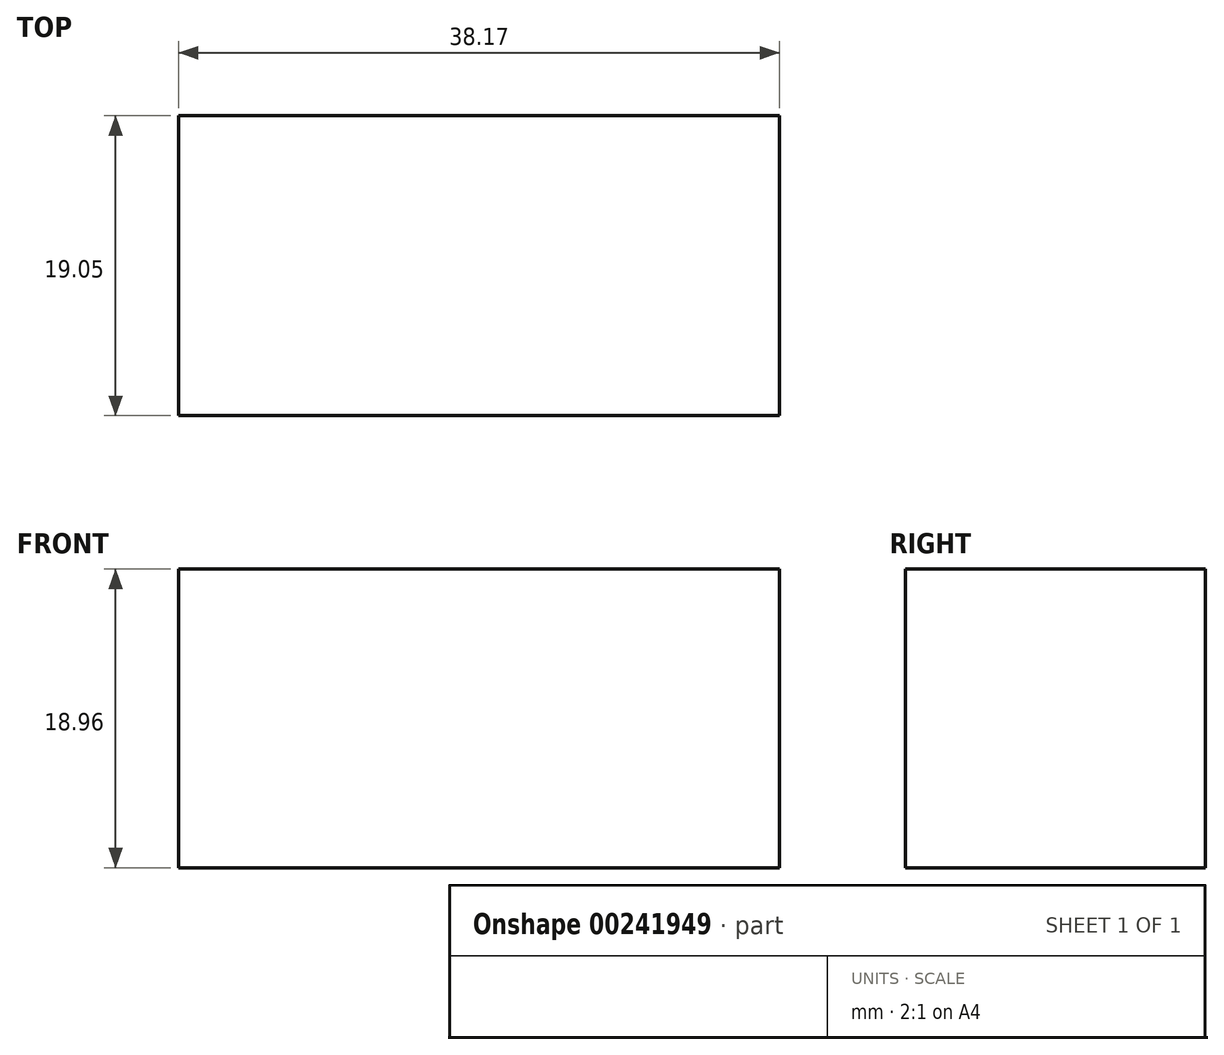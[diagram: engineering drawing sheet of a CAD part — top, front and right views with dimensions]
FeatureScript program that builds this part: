
annotation { "Feature Type Name" : "Feature", "Feature Type Description" : "" }
export const myFeature = defineFeature(function(context is Context, id is Id, definition is map)
    precondition{}
    {
        {
            var Q0;
            Q0=qCreatedBy(makeId("Front.planeOp"),FACE);
            var sketch = newSketch(context, id + "F0", { "sketchPlane" : qUnion([Q0])});
            skLineSegment(sketch, "E0.bottom", {"start": v(-59.43, 59.44) * mm, "end": v(-21.26, 59.44) * mm});
            skLineSegment(sketch, "E0.top", {"start": v(-59.43, 40.48) * mm, "end": v(-21.26, 40.48) * mm});
            skLineSegment(sketch, "E0.left", {"start": v(-59.43, 59.44) * mm, "end": v(-59.43, 40.48) * mm});
            skLineSegment(sketch, "E0.right", {"start": v(-21.26, 59.44) * mm, "end": v(-21.26, 40.48) * mm});
            skSolve(sketch);
        }
        {
            var Q0;
            Q0 = qSketchRegion(id + "F0", true);
            extrude(context, id + "F1", {"entities" : qUnion([Q0]), "depth" : 19.05 * mm});
        }
    });
